AUTODESK INVENTOR PART (.ipt)
format: ipt  version: 2022 (Build 260153000, 153)  size: 105,472 bytes
history: native  units: mm
features: extrude x1, other x1, sketch x1, projected_geometry x1
ambient origin geometry x8: Origin, YZ Plane, XZ Plane, XY Plane, X Axis, Y Axis, Z Axis, Center Point
bodies: Solid1 (feature_tree)
feature tree (4):
  extrude  "Extrusion1"  Depth=3.0mm
  other  "Work Axis1"
  sketch  "Sketch2"  dims[d0=183.747mm d1=6.0mm d2=3.0mm d3=3.0mm d4=8.0mm d5=0.0mm d8=3.0mm d9=81.332mm d12=1000.0mm d13=1000.0mm d14=3.0mm d15=4.2mm]
  projected_geometry  "Projected Loop1"
